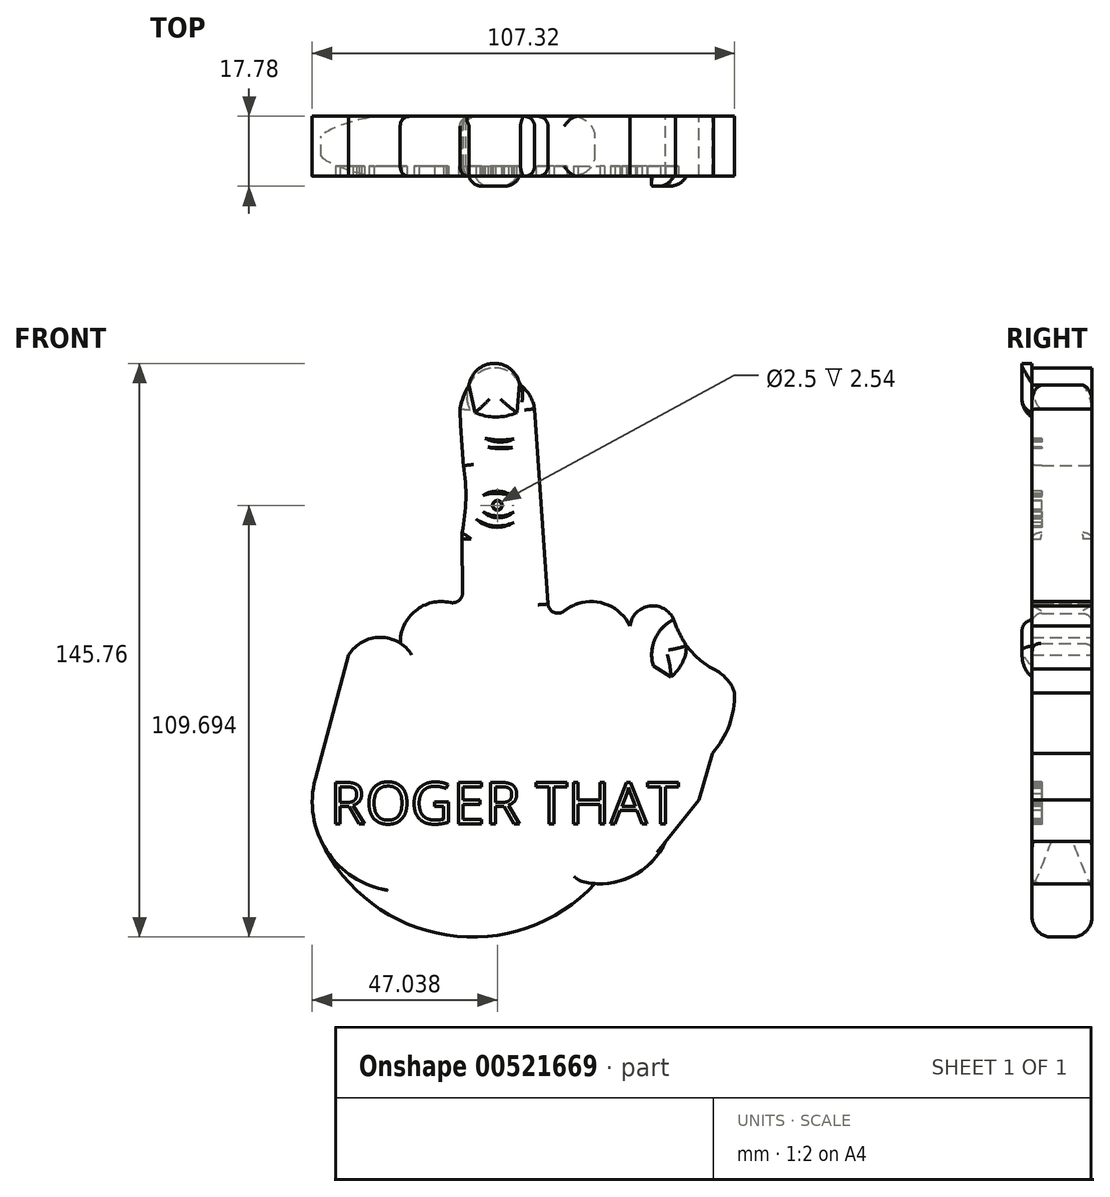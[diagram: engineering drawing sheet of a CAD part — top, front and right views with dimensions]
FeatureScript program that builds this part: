
annotation { "Feature Type Name" : "Feature", "Feature Type Description" : "" }
export const myFeature = defineFeature(function(context is Context, id is Id, definition is map)
    precondition{}
    {
        {
            var Q0;
            Q0=qCreatedBy(makeId("Front.planeOp"),FACE);
            var sketch = newSketch(context, id + "F0", { "sketchPlane" : qUnion([Q0])});
            skLineSegment(sketch, "E0", {"start": v(15.44, -41.79) * mm, "end": v(23.88, -31.3) * mm});
            skLineSegment(sketch, "E1", {"start": v(23.88, -31.3) * mm, "end": v(27.33, -19.44) * mm});
            skArc(sketch, "E2", {"start": v(27.33, -19.44) * mm, "mid": v(31.59, -12.3) * mm, "end": v(32.97, -4.1) * mm});
            skArc(sketch, "E3", {"start": v(32.97, -4.1) * mm, "mid": v(30.92, -0.52) * mm, "end": v(27.59, 1.93) * mm});
            skArc(sketch, "E4", {"start": v(17.92, 12.93) * mm, "mid": v(21.8, 6.59) * mm, "end": v(27.59, 1.93) * mm});
            skArc(sketch, "E5", {"start": v(17.92, 12.93) * mm, "mid": v(12.14, 18.02) * mm, "end": v(6.37, 12.93) * mm});
            skArc(sketch, "E6", {"start": v(6.37, 12.93) * mm, "mid": v(-1.08, 18.82) * mm, "end": v(-10.34, 16.7) * mm});
            skArc(sketch, "E7", {"start": v(-17.89, 68.06) * mm, "mid": v(-19.06, 71.42) * mm, "end": v(-21.43, 74.08) * mm});
            skArc(sketch, "E8", {"start": v(-21.43, 74.08) * mm, "mid": v(-27.98, 78.47) * mm, "end": v(-34.54, 74.08) * mm});
            skArc(sketch, "E9", {"start": v(-34.54, 74.08) * mm, "mid": v(-35.93, 71.16) * mm, "end": v(-36.85, 68.06) * mm});
            skArc(sketch, "E10", {"start": v(-39.27, 18.86) * mm, "mid": v(-48.13, 16.77) * mm, "end": v(-51.98, 8.52) * mm});
            skArc(sketch, "E11", {"start": v(-51.98, 8.52) * mm, "mid": v(-59.13, 9.8) * mm, "end": v(-65.06, 5.6) * mm});
            skLineSegment(sketch, "E12", {"start": v(-65.06, 5.6) * mm, "end": v(-73.57, -25.9) * mm});
            skArc(sketch, "E13", {"start": v(-73.57, -25.9) * mm, "mid": v(-74.26, -33.88) * mm, "end": v(-72.13, -41.62) * mm});
            skArc(sketch, "E14", {"start": v(-2.5, -52.55) * mm, "mid": v(8.16, -50) * mm, "end": v(15.44, -41.79) * mm});
            skArc(sketch, "E15", {"start": v(-72.13, -41.62) * mm, "mid": v(-40.23, -65.63) * mm, "end": v(-2.5, -52.55) * mm});
            skPoint(sketch, "E16.visualSharp", {"position": v(-13.88, 11.64) * mm});
            skArc(sketch, "E16.filletArc", {"start": v(-14.45, 18.47) * mm, "mid": v(-12.92, 16.35) * mm, "end": v(-10.34, 16.7) * mm});
            skPoint(sketch, "E17.visualSharp", {"position": v(-36.13, 17.59) * mm});
            skArc(sketch, "E17.filletArc", {"start": v(-39.27, 18.86) * mm, "mid": v(-37.12, 19.36) * mm, "end": v(-36.17, 21.36) * mm});
            skLineSegment(sketch, "E18", {"start": v(-17.89, 68.06) * mm, "end": v(-14.45, 18.47) * mm});
            skLineSegment(sketch, "E19", {"start": v(-36.17, 21.36) * mm, "end": v(-36.33, 36.41) * mm});
            skArc(sketch, "E20", {"start": v(-36.33, 36.41) * mm, "mid": v(-35.32, 45) * mm, "end": v(-35.95, 53.62) * mm});
            skArc(sketch, "E21", {"start": v(-36.85, 68.06) * mm, "mid": v(-36.48, 60.83) * mm, "end": v(-35.95, 53.62) * mm});
            skPoint(sketch, "E22", {"position": v(-36.25, -66.06) * mm});
            skPoint(sketch, "E22.positionSnap0", {"position": v(-36.25, 28.89) * mm});
            skSolve(sketch);
        }
        {
            var Q0;
            Q0 = qSketchRegion(id + "F0", true);
            extrude(context, id + "F1", {"entities" : qUnion([Q0]), "depth" : 15.24 * mm, "offsetDistance" : 25.4 * mm});
        }
        {
            var Q0;
            Q0=makeQuery(id+"F1.opExtrude","CAP_FACE",FACE,{"disambiguationData":[OSD([sQuery(id+"F0.wireOp",EDGE,"E0"),sQuery(id+"F0.wireOp",EDGE,"E1"),sQuery(id+"F0.wireOp",EDGE,"E2"),sQuery(id+"F0.wireOp",EDGE,"E3"),sQuery(id+"F0.wireOp",EDGE,"E4"),sQuery(id+"F0.wireOp",EDGE,"E5"),sQuery(id+"F0.wireOp",EDGE,"E6"),sQuery(id+"F0.wireOp",EDGE,"GptFBhTJ-q3ag-evlW-NtOx-2fNVeKrcgpSu"),sQuery(id+"F0.wireOp",EDGE,"EpA40aPp-P95g-unbo-Pp6c-kAZiErAJxCPX"),sQuery(id+"F0.wireOp",EDGE,"E7"),sQuery(id+"F0.wireOp",EDGE,"E8"),sQuery(id+"F0.wireOp",EDGE,"E9"),sQuery(id+"F0.wireOp",EDGE,"0ILpLmYA-X21G-Jd7u-k330-Lug129ryTHXt"),sQuery(id+"F0.wireOp",EDGE,"CKYaSEzu-73ww-ZR4T-ithd-3ZRTv4VpGMW0"),sQuery(id+"F0.wireOp",EDGE,"OpZgjSb9-4Cus-1woq-CsCf-FB4qHdjK0wTT"),sQuery(id+"F0.wireOp",EDGE,"E10"),sQuery(id+"F0.wireOp",EDGE,"E11"),sQuery(id+"F0.wireOp",EDGE,"E12"),sQuery(id+"F0.wireOp",EDGE,"E13"),sQuery(id+"F0.wireOp",EDGE,"E14"),sQuery(id+"F0.wireOp",EDGE,"E15")])],"isStart":false});
            var sketch = newSketch(context, id + "F2", { "sketchPlane" : qUnion([Q0])});
            skArc(sketch, "E23", {"start": v(-32.73, 40.1) * mm, "mid": v(-28.07, 38) * mm, "end": v(-23.1, 39.23) * mm});
            skArc(sketch, "E24", {"start": v(-32.73, 40.1) * mm, "mid": v(-28.04, 38.35) * mm, "end": v(-23.1, 39.23) * mm});
            skArc(sketch, "E25", {"start": v(-31.02, 41.98) * mm, "mid": v(-27.08, 40.38) * mm, "end": v(-23.1, 41.9) * mm});
            skArc(sketch, "E26", {"start": v(-31.02, 41.98) * mm, "mid": v(-27.07, 40.83) * mm, "end": v(-23.1, 41.9) * mm});
            skArc(sketch, "E27", {"start": v(-23.1, 45.6) * mm, "mid": v(-27.02, 46.59) * mm, "end": v(-31.02, 46.01) * mm});
            skArc(sketch, "E28", {"start": v(-23.1, 45.6) * mm, "mid": v(-27, 47.15) * mm, "end": v(-31.02, 46.01) * mm});
            skArc(sketch, "E29", {"start": v(-30.44, 60.56) * mm, "mid": v(-26.8, 59.64) * mm, "end": v(-23.1, 60.4) * mm});
            skArc(sketch, "E30", {"start": v(-30.44, 60.56) * mm, "mid": v(-26.78, 60.17) * mm, "end": v(-23.1, 60.4) * mm});
            skCircle(sketch, "E31", {"center": v(-27.31, 43.55) * mm, "radius": 1.25 * mm});
            skCircle(sketch, "E32", {"center": v(-27.31, 43.55) * mm, "radius": 1.1 * mm});
            skArc(sketch, "E33", {"start": v(-29.76, 58.33) * mm, "mid": v(-26.62, 57.94) * mm, "end": v(-23.48, 58.23) * mm});
            skArc(sketch, "E34", {"start": v(-29.76, 58.33) * mm, "mid": v(-26.62, 58.19) * mm, "end": v(-23.48, 58.23) * mm});
            skSolve(sketch);
        }
        {
            var Q0;
            Q0 = qSketchRegion(id + "F2", true);
            extrude(context, id + "F3", {"entities" : qUnion([Q0]), "operationType" : NewBodyOperationType.REMOVE, "oppositeDirection" : true, "depth" : 2.54 * mm, "offsetDistance" : 25.4 * mm});
        }
        {
            var Q0;
            {var subQ0=sQuery(id+"F0.wireOp",EDGE,"E15");var subQ1=sQuery(id+"F0.wireOp",EDGE,"E14");var subQ2=sQuery(id+"F0.wireOp",EDGE,"E13");var subQ3=sQuery(id+"F0.wireOp",EDGE,"E12");var subQ4=sQuery(id+"F0.wireOp",EDGE,"E11");var subQ5=sQuery(id+"F0.wireOp",EDGE,"E10");var subQ6=sQuery(id+"F0.wireOp",EDGE,"OpZgjSb9-4Cus-1woq-CsCf-FB4qHdjK0wTT");var subQ7=sQuery(id+"F0.wireOp",EDGE,"CKYaSEzu-73ww-ZR4T-ithd-3ZRTv4VpGMW0");var subQ8=sQuery(id+"F0.wireOp",EDGE,"0ILpLmYA-X21G-Jd7u-k330-Lug129ryTHXt");var subQ9=sQuery(id+"F0.wireOp",EDGE,"E9");var subQ10=sQuery(id+"F0.wireOp",EDGE,"E8");var subQ11=sQuery(id+"F0.wireOp",EDGE,"E2");var subQ12=sQuery(id+"F0.wireOp",EDGE,"E1");var subQ13=sQuery(id+"F0.wireOp",EDGE,"E3");var subQ14=sQuery(id+"F0.wireOp",EDGE,"E0");var subQ15=sQuery(id+"F0.wireOp",EDGE,"E7");var subQ16=sQuery(id+"F0.wireOp",EDGE,"E4");var subQ17=sQuery(id+"F0.wireOp",EDGE,"E5");var subQ18=sQuery(id+"F0.wireOp",EDGE,"E6");var subQ19=sQuery(id+"F0.wireOp",EDGE,"GptFBhTJ-q3ag-evlW-NtOx-2fNVeKrcgpSu");var subQ20=sQuery(id+"F0.wireOp",EDGE,"EpA40aPp-P95g-unbo-Pp6c-kAZiErAJxCPX");Q0=makeQuery(id+"F3.boolean.opBoolean","SPLIT",FACE,{"disambiguationData":[TD([makeQuery(id+"F1.opExtrude","SWEPT_FACE",FACE,{"disambiguationData":[OSD([subQ14])]})])],"derivedFrom":makeQuery(id+"F1.opExtrude","CAP_FACE",FACE,{"disambiguationData":[OSD([subQ14,subQ12,subQ11,subQ13,subQ16,subQ17,subQ18,subQ19,subQ20,subQ15,subQ10,subQ9,subQ8,subQ7,subQ6,subQ5,subQ4,subQ3,subQ2,subQ1,subQ0])],"isStart":false})});}
            var sketch = newSketch(context, id + "F4", { "sketchPlane" : qUnion([Q0])});
            skArc(sketch, "E35", {"start": v(17.48, 14.53) * mm, "mid": v(12.7, 9.58) * mm, "end": v(12.33, 2.71) * mm});
            skArc(sketch, "E36", {"start": v(17.48, 14.53) * mm, "mid": v(18.9, 11.08) * mm, "end": v(20.76, 7.85) * mm});
            skLineSegment(sketch, "E37", {"start": v(-34.54, 74.08) * mm, "end": v(-33.04, 67.12) * mm});
            skArc(sketch, "E38", {"start": v(-33.04, 67.12) * mm, "mid": v(-27.7, 66.02) * mm, "end": v(-22.34, 67.12) * mm});
            skLineSegment(sketch, "E39", {"start": v(-22.34, 67.12) * mm, "end": v(-21.7, 74.53) * mm});
            skArc(sketch, "E40", {"start": v(-21.7, 74.53) * mm, "mid": v(-28.3, 79.61) * mm, "end": v(-34.54, 74.08) * mm});
            skLineSegment(sketch, "E41", {"start": v(12.33, 2.71) * mm, "end": v(16.8, 0) * mm});
            skArc(sketch, "E42", {"start": v(16.8, 0) * mm, "mid": v(19.65, 3.49) * mm, "end": v(20.76, 7.85) * mm});
            skSolve(sketch);
        }
        {
            var Q0;
            Q0 = qSketchRegion(id + "F4", true);
            extrude(context, id + "F5", {"entities" : qUnion([Q0]), "operationType" : NewBodyOperationType.ADD, "depth" : 2.54 * mm, "offsetDistance" : 25.4 * mm});
        }
        {
            var Q0;
            Q0=makeQuery(id+"F5.opExtrude","CAP_EDGE",EDGE,{"disambiguationData":[OSD([sQuery(id+"F4.wireOp",EDGE,"E38")])],"isStart":false});
            var Q1;
            Q1=makeQuery(id+"F5.opExtrude","CAP_EDGE",EDGE,{"disambiguationData":[OSD([sQuery(id+"F4.wireOp",EDGE,"E37")])],"isStart":false});
            var Q2;
            Q2=makeQuery(id+"F5.opExtrude","CAP_EDGE",EDGE,{"disambiguationData":[OSD([sQuery(id+"F4.wireOp",EDGE,"E39")])],"isStart":false});
            fillet(context, id + "F6", {"entities" : qUnion([Q0, Q1, Q2]), "radius" : 5.08 * mm, "tangentPropagation" : true, "allowEdgeOverflow" : false});
        }
        {
            var Q0;
            Q0=makeQuery(id+"F5.opExtrude","CAP_EDGE",EDGE,{"disambiguationData":[OSD([sQuery(id+"F4.wireOp",EDGE,"E42")])],"isStart":false});
            var Q1;
            Q1=makeQuery(id+"F5.opExtrude","CAP_EDGE",EDGE,{"disambiguationData":[OSD([sQuery(id+"F4.wireOp",EDGE,"E41")])],"isStart":false});
            var Q2;
            Q2=makeQuery(id+"F5.opExtrude","CAP_EDGE",EDGE,{"disambiguationData":[OSD([sQuery(id+"F4.wireOp",EDGE,"E36")])],"isStart":false});
            fillet(context, id + "F7", {"entities" : qUnion([Q0, Q1, Q2]), "radius" : 5.08 * mm, "tangentPropagation" : true, "allowEdgeOverflow" : false});
        }
        {
            var Q0;
            {var subQ0=sQuery(id+"F0.wireOp",EDGE,"E15");var subQ1=makeQuery(id+"F1.opExtrude","SWEPT_FACE",FACE,{"disambiguationData":[OSD([subQ0])]});var subQ2=sQuery(id+"F0.wireOp",EDGE,"E14");var subQ3=makeQuery(id+"F1.opExtrude","SWEPT_FACE",FACE,{"disambiguationData":[OSD([subQ2])]});var subQ4=makeQuery(id+"F3.opExtrude","SWEPT_FACE",FACE,{"disambiguationData":[OSD([sQuery(id+"F2.wireOp",EDGE,"E33")])]});var subQ5=sQuery(id+"F0.wireOp",EDGE,"E13");var subQ6=makeQuery(id+"F1.opExtrude","SWEPT_FACE",FACE,{"disambiguationData":[OSD([subQ5])]});var subQ7=sQuery(id+"F0.wireOp",EDGE,"E12");var subQ8=makeQuery(id+"F1.opExtrude","SWEPT_FACE",FACE,{"disambiguationData":[OSD([subQ7])]});var subQ9=sQuery(id+"F0.wireOp",EDGE,"E11");var subQ10=makeQuery(id+"F1.opExtrude","SWEPT_FACE",FACE,{"disambiguationData":[OSD([subQ9])]});var subQ11=makeQuery(id+"F3.opExtrude","SWEPT_FACE",FACE,{"disambiguationData":[OSD([sQuery(id+"F2.wireOp",EDGE,"E31")])]});var subQ12=sQuery(id+"F0.wireOp",EDGE,"E10");var subQ13=makeQuery(id+"F1.opExtrude","SWEPT_FACE",FACE,{"disambiguationData":[OSD([subQ12])]});var subQ14=makeQuery(id+"F3.opExtrude","SWEPT_FACE",FACE,{"disambiguationData":[OSD([sQuery(id+"F2.wireOp",EDGE,"E30")])]});var subQ15=sQuery(id+"F0.wireOp",EDGE,"OpZgjSb9-4Cus-1woq-CsCf-FB4qHdjK0wTT");var subQ16=makeQuery(id+"F1.opExtrude","SWEPT_FACE",FACE,{"disambiguationData":[OSD([subQ15])]});var subQ17=sQuery(id+"F0.wireOp",EDGE,"CKYaSEzu-73ww-ZR4T-ithd-3ZRTv4VpGMW0");var subQ18=makeQuery(id+"F1.opExtrude","SWEPT_FACE",FACE,{"disambiguationData":[OSD([subQ17])]});var subQ19=makeQuery(id+"F3.opExtrude","SWEPT_FACE",FACE,{"disambiguationData":[OSD([sQuery(id+"F2.wireOp",EDGE,"E29")])]});var subQ20=sQuery(id+"F0.wireOp",EDGE,"0ILpLmYA-X21G-Jd7u-k330-Lug129ryTHXt");var subQ21=makeQuery(id+"F1.opExtrude","SWEPT_FACE",FACE,{"disambiguationData":[OSD([subQ20])]});var subQ22=makeQuery(id+"F3.opExtrude","SWEPT_FACE",FACE,{"disambiguationData":[OSD([sQuery(id+"F2.wireOp",EDGE,"E28")])]});var subQ23=sQuery(id+"F0.wireOp",EDGE,"E9");var subQ24=makeQuery(id+"F1.opExtrude","SWEPT_FACE",FACE,{"disambiguationData":[OSD([subQ23])]});var subQ25=sQuery(id+"F0.wireOp",EDGE,"E8");var subQ26=makeQuery(id+"F1.opExtrude","SWEPT_FACE",FACE,{"disambiguationData":[OSD([subQ25])]});var subQ27=makeQuery(id+"F3.opExtrude","SWEPT_FACE",FACE,{"disambiguationData":[OSD([sQuery(id+"F2.wireOp",EDGE,"E27")])]});var subQ28=sQuery(id+"F0.wireOp",EDGE,"E7");var subQ29=makeQuery(id+"F1.opExtrude","SWEPT_FACE",FACE,{"disambiguationData":[OSD([subQ28])]});var subQ30=makeQuery(id+"F3.opExtrude","SWEPT_FACE",FACE,{"disambiguationData":[OSD([sQuery(id+"F2.wireOp",EDGE,"E26")])]});var subQ31=sQuery(id+"F0.wireOp",EDGE,"E2");var subQ32=makeQuery(id+"F1.opExtrude","SWEPT_FACE",FACE,{"disambiguationData":[OSD([subQ31])]});var subQ33=sQuery(id+"F0.wireOp",EDGE,"E1");var subQ34=makeQuery(id+"F1.opExtrude","SWEPT_FACE",FACE,{"disambiguationData":[OSD([subQ33])]});var subQ35=sQuery(id+"F0.wireOp",EDGE,"EpA40aPp-P95g-unbo-Pp6c-kAZiErAJxCPX");var subQ36=sQuery(id+"F0.wireOp",EDGE,"GptFBhTJ-q3ag-evlW-NtOx-2fNVeKrcgpSu");var subQ37=sQuery(id+"F0.wireOp",EDGE,"E6");var subQ38=sQuery(id+"F0.wireOp",EDGE,"E5");var subQ39=sQuery(id+"F0.wireOp",EDGE,"E4");var subQ40=sQuery(id+"F0.wireOp",EDGE,"E3");var subQ41=sQuery(id+"F0.wireOp",EDGE,"E0");var subQ42=makeQuery(id+"F1.opExtrude","CAP_FACE",FACE,{"disambiguationData":[OSD([subQ41,subQ33,subQ31,subQ40,subQ39,subQ38,subQ37,subQ36,subQ35,subQ28,subQ25,subQ23,subQ20,subQ17,subQ15,subQ12,subQ9,subQ7,subQ5,subQ2,subQ0])],"isStart":false});var subQ43=makeQuery(id+"F1.opExtrude","SWEPT_FACE",FACE,{"disambiguationData":[OSD([subQ41])]});var subQ44=makeQuery(id+"F1.opExtrude","SWEPT_FACE",FACE,{"disambiguationData":[OSD([subQ40])]});var subQ45=makeQuery(id+"F1.opExtrude","SWEPT_FACE",FACE,{"disambiguationData":[OSD([subQ39])]});var subQ46=makeQuery(id+"F3.opExtrude","SWEPT_FACE",FACE,{"disambiguationData":[OSD([sQuery(id+"F2.wireOp",EDGE,"E23")])]});var subQ47=makeQuery(id+"F1.opExtrude","SWEPT_FACE",FACE,{"disambiguationData":[OSD([subQ38])]});var subQ48=makeQuery(id+"F1.opExtrude","SWEPT_FACE",FACE,{"disambiguationData":[OSD([subQ37])]});var subQ49=makeQuery(id+"F3.opExtrude","SWEPT_FACE",FACE,{"disambiguationData":[OSD([sQuery(id+"F2.wireOp",EDGE,"E24")])]});var subQ50=makeQuery(id+"F1.opExtrude","SWEPT_FACE",FACE,{"disambiguationData":[OSD([subQ36])]});var subQ51=makeQuery(id+"F3.opExtrude","SWEPT_FACE",FACE,{"disambiguationData":[OSD([sQuery(id+"F2.wireOp",EDGE,"E25")])]});var subQ52=makeQuery(id+"F1.opExtrude","SWEPT_FACE",FACE,{"disambiguationData":[OSD([subQ35])]});var subQ53=makeQuery(id+"F3.opExtrude","SWEPT_FACE",FACE,{"disambiguationData":[OSD([sQuery(id+"F2.wireOp",EDGE,"E34")])]});var subQ54=sQuery(id+"F4.wireOp",EDGE,"E35");var subQ55=sQuery(id+"F4.wireOp",EDGE,"E42");var subQ56=sQuery(id+"F4.wireOp",EDGE,"E41");var subQ57=sQuery(id+"F4.wireOp",EDGE,"E36");var subQ58=sQuery(id+"F4.wireOp",EDGE,"E37");var subQ59=sQuery(id+"F4.wireOp",EDGE,"E40");var subQ60=sQuery(id+"F4.wireOp",EDGE,"E39");var subQ61=sQuery(id+"F4.wireOp",EDGE,"E38");Q0=makeQuery(id+"F5.boolean.opBoolean","SPLIT",FACE,{"disambiguationData":[TD([subQ43,subQ42,subQ34,subQ32,subQ44,subQ45,subQ47,subQ48,subQ50,subQ52,subQ29,subQ26,subQ24,subQ21,subQ18,subQ16,subQ13,subQ10,subQ8,subQ6,subQ3,subQ1,makeQuery(id+"F3.boolean.opBoolean","COPY",FACE,{"derivedFrom":subQ46}),makeQuery(id+"F3.boolean.opBoolean","COPY",FACE,{"derivedFrom":subQ49}),makeQuery(id+"F3.boolean.opBoolean","COPY",FACE,{"derivedFrom":subQ51}),makeQuery(id+"F3.boolean.opBoolean","COPY",FACE,{"derivedFrom":subQ30}),makeQuery(id+"F3.boolean.opBoolean","COPY",FACE,{"derivedFrom":subQ27}),makeQuery(id+"F3.boolean.opBoolean","COPY",FACE,{"derivedFrom":subQ22}),makeQuery(id+"F3.boolean.opBoolean","COPY",FACE,{"derivedFrom":subQ19}),makeQuery(id+"F3.boolean.opBoolean","COPY",FACE,{"derivedFrom":subQ14}),makeQuery(id+"F3.boolean.opBoolean","COPY",FACE,{"derivedFrom":subQ11}),makeQuery(id+"F3.boolean.opBoolean","COPY",FACE,{"derivedFrom":subQ4}),makeQuery(id+"F3.boolean.opBoolean","COPY",FACE,{"derivedFrom":subQ53}),makeQuery(id+"F5.opExtrude","SWEPT_FACE",FACE,{"disambiguationData":[OSD([subQ54])]}),makeQuery(id+"F5.opExtrude","CAP_FACE",FACE,{"disambiguationData":[OSD([subQ54,subQ57,subQ56,subQ55])],"isStart":true}),makeQuery(id+"F5.opExtrude","SWEPT_FACE",FACE,{"disambiguationData":[OSD([subQ57])]}),makeQuery(id+"F5.opExtrude","SWEPT_FACE",FACE,{"disambiguationData":[OSD([subQ58])]}),makeQuery(id+"F5.opExtrude","CAP_FACE",FACE,{"disambiguationData":[OSD([subQ58,subQ61,subQ60,subQ59])],"isStart":true}),makeQuery(id+"F5.opExtrude","SWEPT_FACE",FACE,{"disambiguationData":[OSD([subQ61])]}),makeQuery(id+"F5.opExtrude","SWEPT_FACE",FACE,{"disambiguationData":[OSD([subQ60])]}),makeQuery(id+"F5.opExtrude","SWEPT_FACE",FACE,{"disambiguationData":[OSD([subQ59])]}),makeQuery(id+"F5.opExtrude","SWEPT_FACE",FACE,{"disambiguationData":[OSD([subQ56])]}),makeQuery(id+"F5.opExtrude","SWEPT_FACE",FACE,{"disambiguationData":[OSD([subQ55])]})])],"derivedFrom":makeQuery(id+"F3.boolean.opBoolean","SPLIT",FACE,{"disambiguationData":[TD([subQ43])],"derivedFrom":subQ42})});}
            var sketch = newSketch(context, id + "F8", { "sketchPlane" : qUnion([Q0])});
            skText(sketch, "E43", { "text": "ROGER THAT", "fontName": "OpenSans-Regular.ttf"});
            const initialGuessF8  = {"E43": [-0.0699, -0.03735, 1, 0, 0.01058]};
            skSetInitialGuess(sketch, initialGuessF8);
            skSolve(sketch);
        }
        {
            var Q0;
            Q0 = qSketchRegion(id + "F8", true);
            extrude(context, id + "F9", {"entities" : qUnion([Q0]), "operationType" : NewBodyOperationType.REMOVE, "oppositeDirection" : true, "depth" : 2.54 * mm, "offsetDistance" : 25.4 * mm});
        }
        {
            var Q0;
            Q0=makeQuery(id+"F1.opExtrude","CAP_EDGE",EDGE,{"disambiguationData":[OSD([sQuery(id+"F0.wireOp",EDGE,"E21")])],"isStart":false});
            var Q1;
            Q1=makeQuery(id+"F1.opExtrude","CAP_EDGE",EDGE,{"disambiguationData":[OSD([sQuery(id+"F0.wireOp",EDGE,"E18")])],"isStart":false});
            var Q2;
            Q2=makeQuery(id+"F1.opExtrude","CAP_EDGE",EDGE,{"disambiguationData":[OSD([sQuery(id+"F0.wireOp",EDGE,"E20")])],"isStart":false});
            var Q3;
            Q3=makeQuery(id+"F1.opExtrude","CAP_EDGE",EDGE,{"disambiguationData":[OSD([sQuery(id+"F0.wireOp",EDGE,"E20")])],"isStart":true});
            var Q4;
            Q4=makeQuery(id+"F1.opExtrude","CAP_EDGE",EDGE,{"disambiguationData":[OSD([sQuery(id+"F0.wireOp",EDGE,"E21")])],"isStart":true});
            var Q5;
            Q5=makeQuery(id+"F1.opExtrude","CAP_EDGE",EDGE,{"disambiguationData":[OSD([sQuery(id+"F0.wireOp",EDGE,"E9")])],"isStart":true});
            var Q6;
            Q6=makeQuery(id+"F1.opExtrude","CAP_EDGE",EDGE,{"disambiguationData":[OSD([sQuery(id+"F0.wireOp",EDGE,"E7")])],"isStart":true});
            var Q7;
            Q7=makeQuery(id+"F1.opExtrude","CAP_EDGE",EDGE,{"disambiguationData":[OSD([sQuery(id+"F0.wireOp",EDGE,"E18")])],"isStart":true});
            var Q8;
            Q8=makeQuery(id+"F1.opExtrude","CAP_EDGE",EDGE,{"disambiguationData":[OSD([sQuery(id+"F0.wireOp",EDGE,"E7")])],"isStart":false});
            fillet(context, id + "F10", {"entities" : qUnion([Q0, Q1, Q2, Q3, Q4, Q5, Q6, Q7, Q8]), "radius" : 2.54 * mm, "tangentPropagation" : true, "allowEdgeOverflow" : false});
        }
        {
            var Q0;
            Q0=makeQuery(id+"F1.opExtrude","CAP_EDGE",EDGE,{"disambiguationData":[OSD([sQuery(id+"F0.wireOp",EDGE,"E19")])],"isStart":false});
            var Q1;
            Q1=makeQuery(id+"F1.opExtrude","CAP_EDGE",EDGE,{"disambiguationData":[OSD([sQuery(id+"F0.wireOp",EDGE,"E19")])],"isStart":true});
            fillet(context, id + "F11", {"entities" : qUnion([Q0, Q1]), "radius" : 2.3 * mm, "tangentPropagation" : true, "allowEdgeOverflow" : false});
        }
        {
            var Q0;
            Q0=makeQuery(id+"F1.opExtrude","CAP_EDGE",EDGE,{"disambiguationData":[OSD([sQuery(id+"F0.wireOp",EDGE,"E15")])],"isStart":false});
            var Q1;
            Q1=makeQuery(id+"F1.opExtrude","CAP_EDGE",EDGE,{"disambiguationData":[OSD([sQuery(id+"F0.wireOp",EDGE,"E15")])],"isStart":true});
            fillet(context, id + "F12", {"entities" : qUnion([Q0, Q1]), "radius" : 5.08 * mm, "tangentPropagation" : true, "allowEdgeOverflow" : false});
        }
        {
            var Q0;
            Q0=makeQuery(id+"F1.opExtrude","CAP_EDGE",EDGE,{"disambiguationData":[OSD([sQuery(id+"F0.wireOp",EDGE,"E14")])],"isStart":true});
            var Q1;
            Q1=makeQuery(id+"F1.opExtrude","CAP_EDGE",EDGE,{"disambiguationData":[OSD([sQuery(id+"F0.wireOp",EDGE,"E14")])],"isStart":false});
            fillet(context, id + "F13", {"entities" : qUnion([Q0, Q1]), "radius" : 0.57 * mm, "tangentPropagation" : true, "allowEdgeOverflow" : false});
        }
    });
